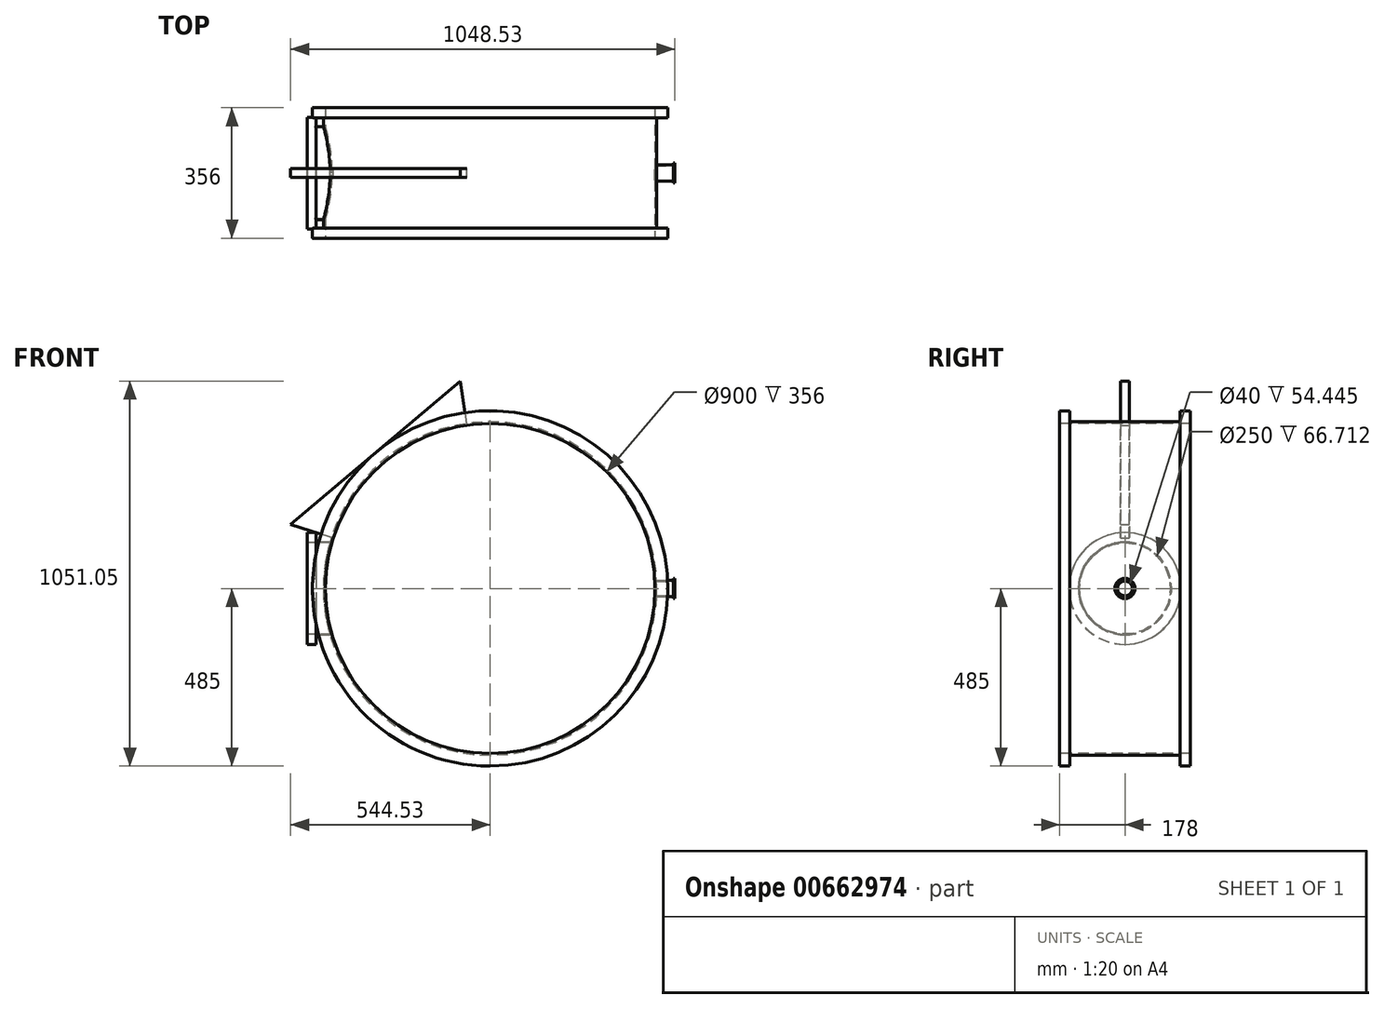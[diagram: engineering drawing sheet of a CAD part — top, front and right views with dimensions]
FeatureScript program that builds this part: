
annotation { "Feature Type Name" : "Feature", "Feature Type Description" : "" }
export const myFeature = defineFeature(function(context is Context, id is Id, definition is map)
    precondition{}
    {
        {
            var Q0;
            Q0=qCreatedBy(makeId("Front.planeOp"),FACE);
            var sketch = newSketch(context, id + "F0", { "sketchPlane" : qUnion([Q0])});
            skCircle(sketch, "E0", {"center": v(0, 0) * mm, "radius": 450 * mm});
            skCircle(sketch, "E1.0", {"center": v(0, 0) * mm, "radius": 455 * mm});
            skSolve(sketch);
        }
        {
            var Q0;
            Q0=makeQuery(id+"F0.imprint","IMPRINT",FACE,{"disambiguationData":[TD([[makeQuery(id+"F0.imprint","IMPRINT",EDGE,{"derivedFrom":sQuery(id+"F0.wireOp",EDGE,"E0")}),-1.0]])]});
            extrude(context, id + "F1", {"entities" : qUnion([Q0]), "endBound" : BoundingType.SYMMETRIC, "oppositeDirection" : true, "depth" : 300 * mm, "offsetDistance" : 25 * mm});
        }
        {
            var Q0;
            Q0=makeQuery(id+"F1.opExtrude","CAP_FACE",FACE,{"disambiguationData":[OSD([sQuery(id+"F0.wireOp",EDGE,"E0"),sQuery(id+"F0.wireOp",EDGE,"E1.0")])],"isStart":false});
            var sketch = newSketch(context, id + "F2", { "sketchPlane" : qUnion([Q0])});
            skCircle(sketch, "E2", {"center": v(0, 0) * mm, "radius": 485 * mm});
            skSolve(sketch);
        }
        {
            var Q0;
            Q0=makeQuery(id+"F2.imprint","IMPRINT",FACE,{"disambiguationData":[TD([[makeQuery(id+"F2.imprint","IMPRINT",EDGE,{"derivedFrom":sQuery(id+"F2.wireOp",EDGE,"E2")}),1.0]])]});
            var Q1;
            Q1=makeQuery(id+"F2.imprint","IMPRINT",FACE,{"disambiguationData":[TD([[makeQuery(id+"F2.imprint","IMPRINT",EDGE,{"derivedFrom":makeQuery(id+"F1.opExtrude","CAP_EDGE",EDGE,{"disambiguationData":[OSD([sQuery(id+"F0.wireOp",EDGE,"E0")])],"isStart":false})}),1.0]])]});
            extrude(context, id + "F3", {"entities" : qUnion([Q0, Q1]), "operationType" : NewBodyOperationType.ADD, "depth" : 28 * mm, "offsetDistance" : 25 * mm});
        }
        {
            var Q0;
            Q0=makeQuery(id+"F1.opExtrude","CAP_FACE",FACE,{"disambiguationData":[OSD([sQuery(id+"F0.wireOp",EDGE,"E0"),sQuery(id+"F0.wireOp",EDGE,"E1.0")])],"isStart":true});
            var sketch = newSketch(context, id + "F4", { "sketchPlane" : qUnion([Q0])});
            skCircle(sketch, "E3", {"center": v(0, 0) * mm, "radius": 485 * mm});
            skSolve(sketch);
        }
        {
            var Q0;
            Q0=makeQuery(id+"F4.imprint","IMPRINT",FACE,{"disambiguationData":[TD([[makeQuery(id+"F4.imprint","IMPRINT",EDGE,{"derivedFrom":sQuery(id+"F4.wireOp",EDGE,"E3")}),1.0]])]});
            var Q1;
            Q1=makeQuery(id+"F4.imprint","IMPRINT",FACE,{"disambiguationData":[TD([[makeQuery(id+"F4.imprint","IMPRINT",EDGE,{"derivedFrom":makeQuery(id+"F1.opExtrude","CAP_EDGE",EDGE,{"disambiguationData":[OSD([sQuery(id+"F0.wireOp",EDGE,"E0")])],"isStart":true})}),-1.0]])]});
            extrude(context, id + "F5", {"entities" : qUnion([Q0, Q1]), "operationType" : NewBodyOperationType.ADD, "depth" : 28 * mm, "offsetDistance" : 25 * mm});
        }
        {
            var Q0;
            Q0=qCreatedBy(makeId("Right.planeOp"),FACE);
            cPlane(context, id + "F6", {"entities" : qUnion([Q0]), "cplaneType" : CPlaneType.OFFSET, "offset" : 500 * mm, "width" : 150 * mm, "height" : 150 * mm});
        }
        {
            var Q0;
            Q0=qCreatedBy(id+"F6.planeOp",FACE);
            var sketch = newSketch(context, id + "F7", { "sketchPlane" : qUnion([Q0])});
            skCircle(sketch, "E4", {"center": v(0, 0) * mm, "radius": 20 * mm});
            skCircle(sketch, "E5", {"center": v(0, 0) * mm, "radius": 22 * mm});
            skLineSegment(sketch, "E6", {"start": v(0, 0) * mm, "end": v(0, 0) * mm});
            skCircle(sketch, "E7", {"center": v(0, 0) * mm, "radius": 27.5 * mm});
            skSolve(sketch);
        }
        {
            var Q0;
            Q0=makeQuery(id+"F7.imprint","IMPRINT",FACE,{"disambiguationData":[TD([[makeQuery(id+"F7.imprint","IMPRINT",EDGE,{"derivedFrom":sQuery(id+"F7.wireOp",EDGE,"E4")}),-1.0]])]});
            extrude(context, id + "F8", {"entities" : qUnion([Q0]), "operationType" : NewBodyOperationType.ADD, "endBound" : BoundingType.UP_TO_NEXT, "oppositeDirection" : true, "depth" : 25 * mm, "offsetDistance" : 25 * mm});
        }
        {
            var Q0;
            Q0=makeQuery(id+"F7.imprint","IMPRINT",FACE,{"disambiguationData":[TD([[makeQuery(id+"F7.imprint","IMPRINT",EDGE,{"derivedFrom":sQuery(id+"F7.wireOp",EDGE,"E4")}),1.0]])]});
            var Q1;
            {var subQ0=sQuery(id+"F0.wireOp",EDGE,"E0");Q1=makeQuery(id+"F5.boolean.opBoolean","MERGE",FACE,{"derivedFrom":[makeQuery(id+"F3.boolean.opBoolean","MERGE",FACE,{"derivedFrom":[makeQuery(id+"F1.opExtrude","SWEPT_FACE",FACE,{"disambiguationData":[OSD([subQ0])]}),makeQuery(id+"F3.opExtrude","SWEPT_FACE",FACE,{"disambiguationData":[OSD([subQ0])]})]}),makeQuery(id+"F5.opExtrude","SWEPT_FACE",FACE,{"disambiguationData":[OSD([subQ0])]})]});}
            extrude(context, id + "F9", {"entities" : qUnion([Q0]), "operationType" : NewBodyOperationType.REMOVE, "endBound" : BoundingType.UP_TO_SURFACE, "oppositeDirection" : true, "depth" : 25 * mm, "endBoundEntityFace" : qUnion([Q1]), "offsetDistance" : 25 * mm});
        }
        {
            var Q0;
            Q0=qCreatedBy(makeId("Right.planeOp"),FACE);
            cPlane(context, id + "F10", {"entities" : qUnion([Q0]), "cplaneType" : CPlaneType.OFFSET, "offset" : 475 * mm, "oppositeDirection" : true, "width" : 150 * mm, "height" : 150 * mm});
        }
        {
            var Q0;
            Q0=qCreatedBy(id+"F10.planeOp",FACE);
            var sketch = newSketch(context, id + "F11", { "sketchPlane" : qUnion([Q0])});
            skCircle(sketch, "E8", {"center": v(0, 0) * mm, "radius": 125 * mm});
            skCircle(sketch, "E9", {"center": v(0, 0) * mm, "radius": 127 * mm});
            skCircle(sketch, "E10", {"center": v(0, 0) * mm, "radius": 152.5 * mm});
            skLineSegment(sketch, "E11", {"start": v(0, 0) * mm, "end": v(0, 0) * mm});
            skSolve(sketch);
        }
        {
            var Q0;
            Q0=makeQuery(id+"F11.imprint","IMPRINT",FACE,{"disambiguationData":[TD([[makeQuery(id+"F11.imprint","IMPRINT",EDGE,{"derivedFrom":sQuery(id+"F11.wireOp",EDGE,"E8")}),-1.0]])]});
            extrude(context, id + "F12", {"entities" : qUnion([Q0]), "operationType" : NewBodyOperationType.ADD, "endBound" : BoundingType.UP_TO_NEXT, "depth" : 25 * mm, "offsetDistance" : 25 * mm});
        }
        {
            var Q0;
            Q0=makeQuery(id+"F11.imprint","IMPRINT",FACE,{"disambiguationData":[TD([[makeQuery(id+"F11.imprint","IMPRINT",EDGE,{"derivedFrom":sQuery(id+"F11.wireOp",EDGE,"E8")}),1.0]])]});
            var Q1;
            {var subQ0=sQuery(id+"F0.wireOp",EDGE,"E0");Q1=makeQuery(id+"F5.boolean.opBoolean","MERGE",FACE,{"derivedFrom":[makeQuery(id+"F3.boolean.opBoolean","MERGE",FACE,{"derivedFrom":[makeQuery(id+"F1.opExtrude","SWEPT_FACE",FACE,{"disambiguationData":[OSD([subQ0])]}),makeQuery(id+"F3.opExtrude","SWEPT_FACE",FACE,{"disambiguationData":[OSD([subQ0])]})]}),makeQuery(id+"F5.opExtrude","SWEPT_FACE",FACE,{"disambiguationData":[OSD([subQ0])]})]});}
            extrude(context, id + "F13", {"entities" : qUnion([Q0]), "operationType" : NewBodyOperationType.REMOVE, "endBound" : BoundingType.UP_TO_SURFACE, "depth" : 25 * mm, "endBoundEntityFace" : qUnion([Q1]), "offsetDistance" : 25 * mm});
        }
        {
            var Q0;
            Q0=makeQuery(id+"F11.imprint","IMPRINT",FACE,{"disambiguationData":[TD([[makeQuery(id+"F11.imprint","IMPRINT",EDGE,{"derivedFrom":sQuery(id+"F11.wireOp",EDGE,"E9")}),-1.0]])]});
            var Q1;
            Q1=makeQuery(id+"F11.imprint","IMPRINT",FACE,{"disambiguationData":[TD([[makeQuery(id+"F11.imprint","IMPRINT",EDGE,{"derivedFrom":sQuery(id+"F11.wireOp",EDGE,"E8")}),-1.0]])]});
            extrude(context, id + "F14", {"entities" : qUnion([Q0, Q1]), "operationType" : NewBodyOperationType.ADD, "oppositeDirection" : true, "depth" : 24 * mm, "offsetDistance" : 25 * mm});
        }
        {
            var Q0;
            Q0=makeQuery(id+"F7.imprint","IMPRINT",FACE,{"disambiguationData":[TD([[makeQuery(id+"F7.imprint","IMPRINT",EDGE,{"derivedFrom":sQuery(id+"F7.wireOp",EDGE,"E5")}),-1.0]])]});
            var Q1;
            Q1=makeQuery(id+"F7.imprint","IMPRINT",FACE,{"disambiguationData":[TD([[makeQuery(id+"F7.imprint","IMPRINT",EDGE,{"derivedFrom":sQuery(id+"F7.wireOp",EDGE,"E4")}),-1.0]])]});
            extrude(context, id + "F15", {"entities" : qUnion([Q0, Q1]), "operationType" : NewBodyOperationType.ADD, "depth" : 4 * mm, "offsetDistance" : 25 * mm});
        }
        {
            var Q0;
            Q0=qCreatedBy(makeId("Front.planeOp"),FACE);
            var sketch = newSketch(context, id + "F16", { "sketchPlane" : qUnion([Q0])});
            skLineSegment(sketch, "E12", {"start": v(0, 0) * mm, "end": v(-475, 152.5) * mm, "construction": true});
            skLineSegment(sketch, "E13", {"start": v(0, 0) * mm, "end": v(-313.05, 370.44) * mm, "construction": true});
            skLineSegment(sketch, "E14", {"start": v(-313.05, 370.44) * mm, "end": v(-81.58, 566.05) * mm});
            skLineSegment(sketch, "E15", {"start": v(-313.05, 370.44) * mm, "end": v(-544.53, 174.82) * mm});
            skLineSegment(sketch, "E16", {"start": v(-475, 152.5) * mm, "end": v(-544.53, 174.82) * mm});
            skLineSegment(sketch, "E17", {"start": v(-69.18, 480.04) * mm, "end": v(-81.58, 566.05) * mm});
            skLineSegment(sketch, "E18", {"start": v(-69.18, 480.04) * mm, "end": v(-64.19, 445.4) * mm});
            skLineSegment(sketch, "E19", {"start": v(-475, 152.5) * mm, "end": v(-428.46, 137.56) * mm});
            skArc(sketch, "E20", {"start": v(-428.46, 137.56) * mm, "mid": v(-290.46, 343.7) * mm, "end": v(-64.19, 445.4) * mm});
            skLineSegment(sketch, "E21", {"start": v(-64.19, 445.4) * mm, "end": v(0, 0) * mm, "construction": true});
            skSolve(sketch);
        }
        {
            var Q0;
            Q0=makeQuery(id+"F16.imprint","IMPRINT",FACE,{"disambiguationData":[TD([[makeQuery(id+"F16.imprint","IMPRINT",EDGE,{"derivedFrom":sQuery(id+"F16.wireOp",EDGE,"E14")}),-1.0]])]});
            extrude(context, id + "F17", {"entities" : qUnion([Q0]), "endBound" : BoundingType.SYMMETRIC, "depth" : 25 * mm, "offsetDistance" : 25 * mm});
        }
    });
